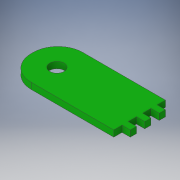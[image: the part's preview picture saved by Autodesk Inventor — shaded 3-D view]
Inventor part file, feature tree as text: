
AUTODESK INVENTOR PART (.ipt)
format: ipt  version: 2019.1 (Build 231200000, 200)  size: 135,680 bytes
history: native  units: in
note: dims shown in document units (in); Inventor stores cm internally (conversion verified against a paired STEP export)
features: extrude x1, sketch x1
ambient origin geometry x8: Origin, YZ Plane, XZ Plane, XY Plane, X Axis, Y Axis, Z Axis, Center Point
bodies: Body1 (feature_tree)
feature tree (2):
  extrude  "Extrusion7"  Depth=0.1378in
  sketch  "Sketch1"  dims[d2=0.2362in d5=0.1378in d15=0.0in d26=0.0787in d27=0.0787in d28=0.0787in d29=0.0787in d30=0.0787in d31=0.0787in d32=0.0591in d33=0.0591in d34=0.0787in d35=0.0591in d36=0.0787in d37=0.06in d38=0.0in d39=0.7874in]
